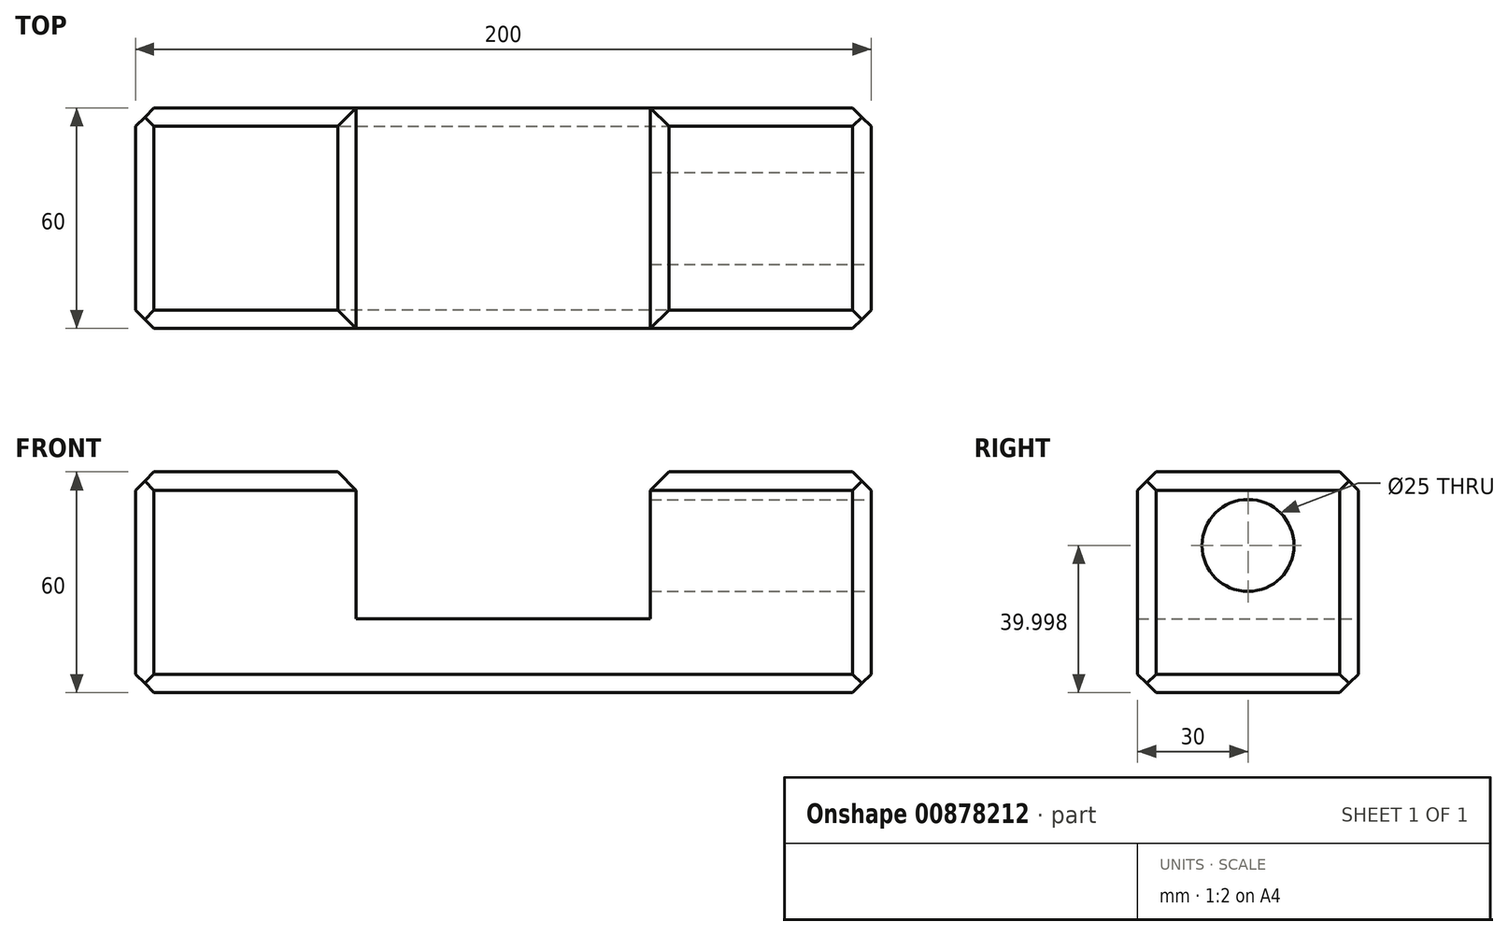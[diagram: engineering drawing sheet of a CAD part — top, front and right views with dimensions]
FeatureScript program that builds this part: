
annotation { "Feature Type Name" : "Feature", "Feature Type Description" : "" }
export const myFeature = defineFeature(function(context is Context, id is Id, definition is map)
    precondition{}
    {
        {
            var Q0;
            Q0=qCreatedBy(makeId("Front.planeOp"),FACE);
            var sketch = newSketch(context, id + "F0", { "sketchPlane" : qUnion([Q0])});
            skLineSegment(sketch, "E0", {"start": v(-67.15, 28.7) * mm, "end": v(-7.15, 28.7) * mm});
            skLineSegment(sketch, "E1", {"start": v(-7.15, 28.7) * mm, "end": v(-7.15, -11.3) * mm});
            skLineSegment(sketch, "E2", {"start": v(-7.15, -11.3) * mm, "end": v(72.85, -11.3) * mm});
            skLineSegment(sketch, "E3", {"start": v(72.85, -11.3) * mm, "end": v(72.85, 28.7) * mm});
            skLineSegment(sketch, "E4", {"start": v(72.85, 28.7) * mm, "end": v(132.85, 28.7) * mm});
            skLineSegment(sketch, "E5", {"start": v(132.85, 28.7) * mm, "end": v(132.85, -31.3) * mm});
            skLineSegment(sketch, "E6", {"start": v(132.85, -31.3) * mm, "end": v(-67.15, -31.3) * mm});
            skLineSegment(sketch, "E7", {"start": v(-67.15, -31.3) * mm, "end": v(-67.15, 28.7) * mm});
            skSolve(sketch);
        }
        {
            var Q0;
            Q0=makeQuery(id+"F0.imprint","IMPRINT",FACE,{"disambiguationData":[TD([[makeQuery(id+"F0.imprint","IMPRINT",EDGE,{"derivedFrom":sQuery(id+"F0.wireOp",EDGE,"E0")}),-1.0]])]});
            extrude(context, id + "F1", {"entities" : qUnion([Q0]), "depth" : 60 * mm, "offsetDistance" : 25 * mm});
        }
        {
            var Q0;
            Q0=makeQuery(id+"F1.opExtrude","SWEPT_FACE",FACE,{"disambiguationData":[OSD([sQuery(id+"F0.wireOp",EDGE,"E5")])]});
            var sketch = newSketch(context, id + "F2", { "sketchPlane" : qUnion([Q0])});
            skCircle(sketch, "E8", {"center": v(-30, 8.7) * mm, "radius": 12.5 * mm});
            skSolve(sketch);
        }
        {
            var Q0;
            Q0=makeQuery(id+"F2.imprint","IMPRINT",FACE,{"disambiguationData":[TD([[makeQuery(id+"F2.imprint","IMPRINT",EDGE,{"derivedFrom":sQuery(id+"F2.wireOp",EDGE,"E8")}),1.0]])]});
            extrude(context, id + "F3", {"entities" : qUnion([Q0]), "operationType" : NewBodyOperationType.REMOVE, "oppositeDirection" : true, "depth" : 99 * mm, "offsetDistance" : 25 * mm});
        }
        {
            var Q0;
            Q0=makeQuery(id+"F1.opExtrude","CAP_EDGE",EDGE,{"disambiguationData":[OSD([sQuery(id+"F0.wireOp",EDGE,"E7")])],"isStart":false});
            var Q1;
            Q1=makeQuery(id+"F1.opExtrude","CAP_EDGE",EDGE,{"disambiguationData":[OSD([sQuery(id+"F0.wireOp",EDGE,"E7")])],"isStart":true});
            chamfer(context, id + "F4", {"entities" : qUnion([Q0, Q1]), "width" : 5 * mm, "tangentPropagation" : true});
        }
        {
            var Q0;
            Q0=makeQuery(id+"F1.opExtrude","CAP_EDGE",EDGE,{"disambiguationData":[OSD([sQuery(id+"F0.wireOp",EDGE,"E6")])],"isStart":false});
            var Q1;
            Q1=makeQuery(id+"F1.opExtrude","SWEPT_EDGE",EDGE,{"disambiguationData":[OSD([sQuery(id+"F0.wireOp",EDGE,"E6"),sQuery(id+"F0.wireOp",EDGE,"E7")])]});
            chamfer(context, id + "F5", {"entities" : qUnion([Q0, Q1]), "width" : 5 * mm, "tangentPropagation" : true});
        }
        {
            var Q0;
            Q0=makeQuery(id+"F1.opExtrude","SWEPT_EDGE",EDGE,{"disambiguationData":[OSD([sQuery(id+"F0.wireOp",EDGE,"E0"),sQuery(id+"F0.wireOp",EDGE,"E7")])]});
            var Q1;
            Q1=makeQuery(id+"F1.opExtrude","SWEPT_EDGE",EDGE,{"disambiguationData":[OSD([sQuery(id+"F0.wireOp",EDGE,"E4"),sQuery(id+"F0.wireOp",EDGE,"E5")])]});
            var Q2;
            Q2=makeQuery(id+"F1.opExtrude","CAP_EDGE",EDGE,{"disambiguationData":[OSD([sQuery(id+"F0.wireOp",EDGE,"E4")])],"isStart":true});
            var Q3;
            Q3=makeQuery(id+"F1.opExtrude","CAP_EDGE",EDGE,{"disambiguationData":[OSD([sQuery(id+"F0.wireOp",EDGE,"E4")])],"isStart":false});
            var Q4;
            Q4=makeQuery(id+"F1.opExtrude","SWEPT_EDGE",EDGE,{"disambiguationData":[OSD([sQuery(id+"F0.wireOp",EDGE,"E3"),sQuery(id+"F0.wireOp",EDGE,"E4")])]});
            var Q5;
            Q5=makeQuery(id+"F1.opExtrude","CAP_EDGE",EDGE,{"disambiguationData":[OSD([sQuery(id+"F0.wireOp",EDGE,"E6")])],"isStart":true});
            chamfer(context, id + "F6", {"entities" : qUnion([Q0, Q1, Q2, Q3, Q4, Q5]), "width" : 5 * mm, "tangentPropagation" : true});
        }
        {
            var Q0;
            Q0=makeQuery(id+"F1.opExtrude","CAP_EDGE",EDGE,{"disambiguationData":[OSD([sQuery(id+"F0.wireOp",EDGE,"E5")])],"isStart":false});
            var Q1;
            Q1=makeQuery(id+"F1.opExtrude","CAP_EDGE",EDGE,{"disambiguationData":[OSD([sQuery(id+"F0.wireOp",EDGE,"E5")])],"isStart":true});
            var Q2;
            Q2=makeQuery(id+"F1.opExtrude","SWEPT_EDGE",EDGE,{"disambiguationData":[OSD([sQuery(id+"F0.wireOp",EDGE,"E5"),sQuery(id+"F0.wireOp",EDGE,"E6")])]});
            var Q3;
            Q3=makeQuery(id+"F1.opExtrude","SWEPT_EDGE",EDGE,{"disambiguationData":[OSD([sQuery(id+"F0.wireOp",EDGE,"E0"),sQuery(id+"F0.wireOp",EDGE,"E1")])]});
            var Q4;
            Q4=makeQuery(id+"F1.opExtrude","CAP_EDGE",EDGE,{"disambiguationData":[OSD([sQuery(id+"F0.wireOp",EDGE,"E0")])],"isStart":false});
            var Q5;
            Q5=makeQuery(id+"F1.opExtrude","CAP_EDGE",EDGE,{"disambiguationData":[OSD([sQuery(id+"F0.wireOp",EDGE,"E0")])],"isStart":true});
            chamfer(context, id + "F7", {"entities" : qUnion([Q0, Q1, Q2, Q3, Q4, Q5]), "width" : 5 * mm, "tangentPropagation" : true});
        }
    });
